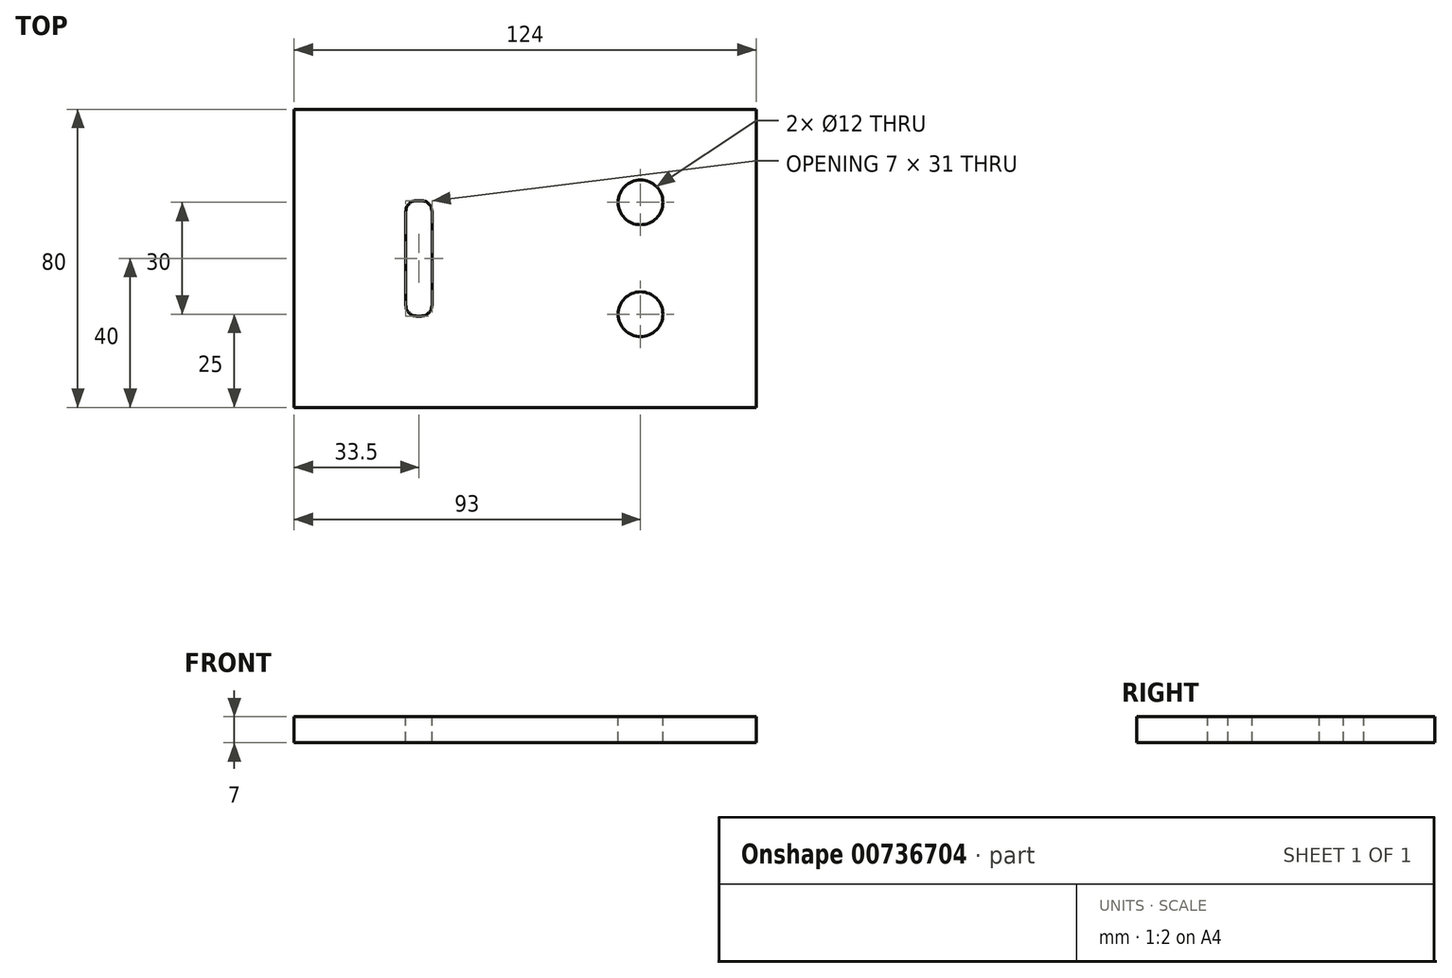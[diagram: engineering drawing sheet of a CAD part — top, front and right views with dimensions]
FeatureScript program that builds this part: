
annotation { "Feature Type Name" : "Feature", "Feature Type Description" : "" }
export const myFeature = defineFeature(function(context is Context, id is Id, definition is map)
    precondition{}
    {
        {
            var Q0;
            Q0=qCreatedBy(makeId("Top.planeOp"),FACE);
            var sketch = newSketch(context, id + "F0", { "sketchPlane" : qUnion([Q0])});
            skLineSegment(sketch, "E0.bottom", {"start": v(0, 0) * mm, "end": v(-124, 0) * mm});
            skLineSegment(sketch, "E0.top", {"start": v(0, 80) * mm, "end": v(-124, 80) * mm});
            skLineSegment(sketch, "E0.left", {"start": v(0, 0) * mm, "end": v(0, 80) * mm});
            skLineSegment(sketch, "E0.right", {"start": v(-124, 0) * mm, "end": v(-124, 80) * mm});
            skSolve(sketch);
        }
        {
            var Q0;
            Q0=makeQuery(id+"F0.imprint","IMPRINT",FACE,{"disambiguationData":[TD([[makeQuery(id+"F0.imprint","IMPRINT",EDGE,{"derivedFrom":sQuery(id+"F0.wireOp",EDGE,"E0.bottom")}),-1.0]])]});
            extrude(context, id + "F1", {"entities" : qUnion([Q0]), "depth" : 7 * mm, "offsetDistance" : 25 * mm});
        }
        {
            var Q0;
            Q0=makeQuery(id+"F1.opExtrude","CAP_FACE",FACE,{"disambiguationData":[OSD([sQuery(id+"F0.wireOp",EDGE,"E0.bottom"),sQuery(id+"F0.wireOp",EDGE,"E0.top"),sQuery(id+"F0.wireOp",EDGE,"E0.left"),sQuery(id+"F0.wireOp",EDGE,"E0.right")])],"isStart":false});
            var sketch = newSketch(context, id + "F2", { "sketchPlane" : qUnion([Q0])});
            skLineSegment(sketch, "E1", {"start": v(-62, 0) * mm, "end": v(-62, 80) * mm});
            skLineSegment(sketch, "E2", {"start": v(-31, 40) * mm, "end": v(-31, 25) * mm});
            skLineSegment(sketch, "E3", {"start": v(-31, 25) * mm, "end": v(-31, 55) * mm});
            skCircle(sketch, "E4", {"center": v(-31, 55) * mm, "radius": 6 * mm});
            skCircle(sketch, "E5", {"center": v(-31, 25) * mm, "radius": 6 * mm});
            skSolve(sketch);
        }
        {
            var Q0;
            Q0=makeQuery(id+"F2.imprint","IMPRINT",FACE,{"disambiguationData":[TD([[makeQuery(id+"F2.imprint","IMPRINT",EDGE,{"derivedFrom":sQuery(id+"F2.wireOp",EDGE,"E4")}),1.0]])]});
            var Q1;
            Q1=makeQuery(id+"F2.imprint","IMPRINT",FACE,{"disambiguationData":[TD([[makeQuery(id+"F2.imprint","IMPRINT",EDGE,{"derivedFrom":sQuery(id+"F2.wireOp",EDGE,"E5")}),1.0]])]});
            extrude(context, id + "F3", {"entities" : qUnion([Q0, Q1]), "operationType" : NewBodyOperationType.REMOVE, "oppositeDirection" : true, "depth" : 25 * mm, "offsetDistance" : 25 * mm});
        }
        {
            var Q0;
            Q0=makeQuery(id+"F1.opExtrude","CAP_FACE",FACE,{"disambiguationData":[OSD([sQuery(id+"F0.wireOp",EDGE,"E0.bottom"),sQuery(id+"F0.wireOp",EDGE,"E0.top"),sQuery(id+"F0.wireOp",EDGE,"E0.left"),sQuery(id+"F0.wireOp",EDGE,"E0.right")])],"isStart":false});
            var sketch = newSketch(context, id + "F4", { "sketchPlane" : qUnion([Q0])});
            skLineSegment(sketch, "E6", {"start": v(-94, 40) * mm, "end": v(-94, 55.5) * mm});
            skLineSegment(sketch, "E7", {"start": v(-94, 55.5) * mm, "end": v(-94, 24.5) * mm});
            skLineSegment(sketch, "E8", {"start": v(-94, 24.5) * mm, "end": v(-87, 24.5) * mm});
            skLineSegment(sketch, "E9", {"start": v(-87, 24.5) * mm, "end": v(-87, 55.5) * mm});
            skLineSegment(sketch, "E10", {"start": v(-94, 55.5) * mm, "end": v(-87, 55.5) * mm});
            skSolve(sketch);
        }
        {
            var Q0;
            {var subQ0=sQuery(id+"F4.wireOp",EDGE,"E8");Q0=makeQuery(id+"F4.imprint","IMPRINT",FACE,{"disambiguationData":[TD([[makeQuery(id+"F4.imprint","IMPRINT",EDGE,{"derivedFrom":subQ0}),1.0]])]});}
            extrude(context, id + "F5", {"entities" : qUnion([Q0]), "operationType" : NewBodyOperationType.REMOVE, "oppositeDirection" : true, "depth" : 25 * mm, "offsetDistance" : 25 * mm});
        }
        {
            var Q0;
            Q0=makeQuery(id+"F5.boolean.opBoolean","COPY",EDGE,{"derivedFrom":makeQuery(id+"F5.opExtrude","SWEPT_EDGE",EDGE,{"disambiguationData":[OSD([sQuery(id+"F4.wireOp",EDGE,"E9"),sQuery(id+"F4.wireOp",EDGE,"E10")])]})});
            var Q1;
            Q1=makeQuery(id+"F5.boolean.opBoolean","COPY",EDGE,{"derivedFrom":makeQuery(id+"F5.opExtrude","SWEPT_EDGE",EDGE,{"disambiguationData":[OSD([sQuery(id+"F4.wireOp",EDGE,"E7"),sQuery(id+"F4.wireOp",EDGE,"E10")])]})});
            var Q2;
            Q2=makeQuery(id+"F5.boolean.opBoolean","COPY",EDGE,{"derivedFrom":makeQuery(id+"F5.opExtrude","SWEPT_EDGE",EDGE,{"disambiguationData":[OSD([sQuery(id+"F4.wireOp",EDGE,"E8"),sQuery(id+"F4.wireOp",EDGE,"E9")])]})});
            var Q3;
            Q3=makeQuery(id+"F5.boolean.opBoolean","COPY",EDGE,{"derivedFrom":makeQuery(id+"F5.opExtrude","SWEPT_EDGE",EDGE,{"disambiguationData":[OSD([sQuery(id+"F4.wireOp",EDGE,"E7"),sQuery(id+"F4.wireOp",EDGE,"E8")])]})});
            fillet(context, id + "F6", {"entities" : qUnion([Q0, Q1, Q2, Q3]), "radius" : 2.9 * mm, "tangentPropagation" : true, "allowEdgeOverflow" : false});
        }
    });
